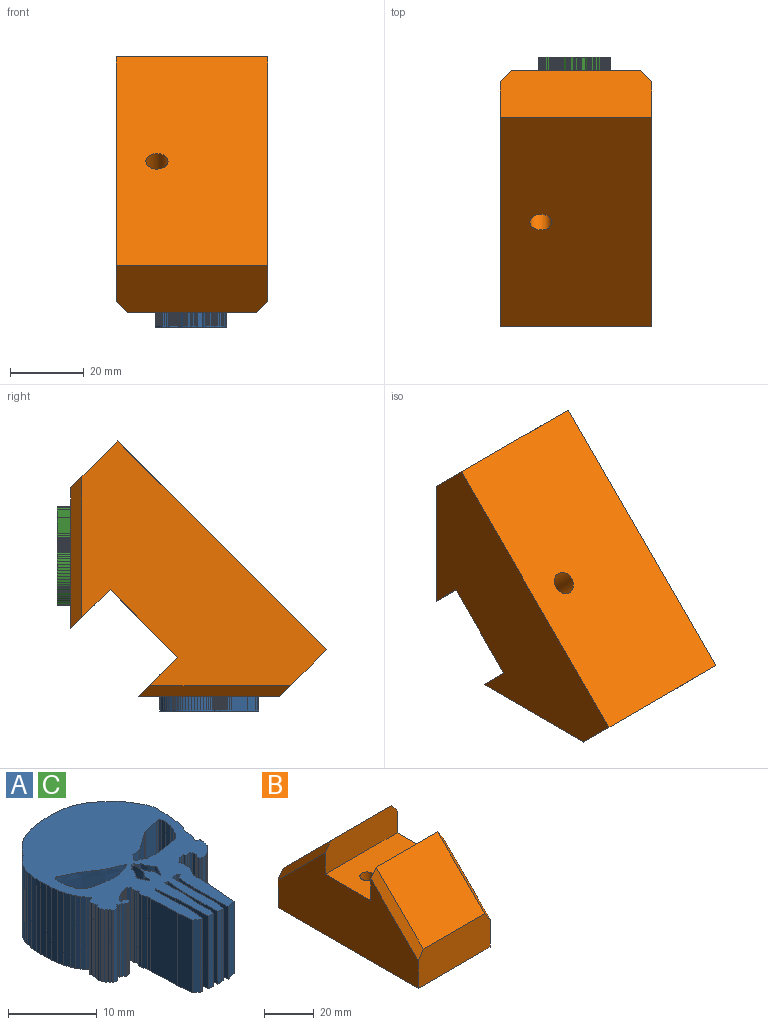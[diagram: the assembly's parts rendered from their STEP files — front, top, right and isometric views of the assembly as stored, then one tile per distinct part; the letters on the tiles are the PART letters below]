
ASSEMBLY  parts=3 mates=2
PART A: 224 faces, bbox 19.4x26.7x10 mm
  f0: plane 10x0.29mm, normal (0.2,0.98,0), area 3mm2, adj f1,f221,f222,f223
  f1: plane 10x0.83mm, normal (0.02,1,0), area 8.3mm2, adj f0,f2,f222,f223
  f2: plane 10x0.89mm, normal (0.48,0.88,0), area 10.2mm2, adj f1,f3,f222,f223
  f3: plane 10x0.29mm, normal (0.2,0.98,0), area 3mm2, adj f2,f4,f222,f223
  f4: plane 10x0.21mm, normal (0.5,0.87,0), area 2.4mm2, adj f3,f5,f222,f223
  f5: plane 10x0.29mm, normal (0.91,-0.42,0), area 3.2mm2, adj f4,f6,f222,f223
  f6: plane 10x0.67mm, normal (0.78,-0.63,0), area 8.6mm2, adj f5,f7,f222,f223
  f7: plane 10x1.25mm, normal (0.11,-0.99,0), area 12.6mm2, adj f6,f8,f222,f223
  f8: plane 10x2.46mm, normal (0.59,-0.81,0), area 30.5mm2, adj f7,f9,f222,f223
  f9: plane 10x0.51mm, normal (0.5,-0.87,0), area 5.9mm2, adj f8,f10,f222,f223
  f10: plane 10x2.19mm, normal (0.22,-0.98,0), area 22.4mm2, adj f9,f11,f222,f223
  f11: plane 10x0.54mm, normal (0.32,-0.95,0), area 5.7mm2, adj f10,f12,f222,f223
  f12: plane 10x0.41mm, normal (-0.94,-0.34,0), area 4.4mm2, adj f11,f13,f222,f223
  f13: plane 10x0.54mm, normal (-1,-0.08,0), area 5.4mm2, adj f12,f14,f222,f223
  f14: plane 10x0.97mm, normal (-0.99,0.12,0), area 9.7mm2, adj f13,f15,f222,f223
  f15: plane 10x0.7mm, normal (-0.92,0.38,0), area 7.6mm2, adj f14,f16,f222,f223
  f16: plane 10x0.26mm, normal (-0.79,0.61,0), area 3.3mm2, adj f15,f17,f222,f223
  f17: plane 10x0.69mm, normal (-0.88,0.47,0), area 7.8mm2, adj f16,f18,f222,f223
  f18: plane 10x0.56mm, normal (-0.67,0.75,0), area 7.4mm2, adj f17,f19,f222,f223
  f19: plane 10x0.72mm, normal (-0.22,0.98,0), area 7.3mm2, adj f18,f20,f222,f223
  f20: plane 10x0.7mm, normal (-0.12,0.99,0), area 7.1mm2, adj f19,f21,f222,f223
  f21: plane 10x1.19mm, normal (-0.18,0.98,0), area 12.1mm2, adj f20,f22,f222,f223
  f22: plane 10x0.7mm, normal (-0.12,0.99,0), area 7.1mm2, adj f21,f221,f222,f223
  f23: plane 10x0.35mm, normal (-0.2,-0.98,0), area 3.6mm2, adj f24,f217,f222,f223
  f24: plane 10x0.24mm, normal (-0.61,-0.79,0), area 3mm2, adj f23,f25,f222,f223
  f25: plane 10x0.19mm, normal (-0.67,-0.74,0), area 2.6mm2, adj f24,f26,f222,f223
  f26: plane 10x0.17mm, normal (-0.2,-0.98,0), area 1.8mm2, adj f25,f27,f222,f223
  f27: plane 10x0.2mm, normal (0.43,-0.9,0), area 2.2mm2, adj f26,f28,f222,f223
  f28: plane 10x0.15mm, normal (0.38,-0.93,0), area 1.6mm2, adj f27,f29,f222,f223
  f29: plane 10x0.16mm, normal (0.75,-0.66,0), area 2.1mm2, adj f28,f30,f222,f223
  f30: plane 10x0.29mm, normal (0.95,0.32,0), area 3mm2, adj f29,f31,f222,f223
  f31: plane 10x0.13mm, normal (0.86,0.51,0), area 1.5mm2, adj f30,f32,f222,f223
  f32: plane 10x0.53mm, normal (0.08,1,0), area 5.3mm2, adj f31,f33,f222,f223
  f33: plane 10x0.21mm, normal (0.83,0.56,0), area 2.5mm2, adj f32,f34,f222,f223
  f34: plane 10x0.34mm, normal (0.71,-0.71,0), area 4.8mm2, adj f33,f35,f222,f223
  f35: plane 10x0.17mm, normal (0.67,-0.75,0), area 2.2mm2, adj f34,f36,f222,f223
  f36: plane 10x0.11mm, normal (0.71,-0.71,0), area 1.6mm2, adj f35,f37,f222,f223
  f37: plane 10x0.41mm, normal (0.5,-0.87,0), area 4.7mm2, adj f36,f38,f222,f223
  f38: plane 10x0.21mm, normal (0.55,-0.83,0), area 2.5mm2, adj f37,f39,f222,f223
  f39: plane 10x0.25mm, normal (0.46,-0.89,0), area 2.8mm2, adj f38,f40,f222,f223
  f40: plane 10x0.24mm, normal (0.33,-0.94,0), area 2.6mm2, adj f39,f41,f222,f223
  f41: plane 10x0.28mm, normal (0.12,-0.99,0), area 2.8mm2, adj f40,f42,f222,f223
  f42: plane 10x0.2mm, normal (0.43,-0.9,0), area 2.2mm2, adj f41,f43,f222,f223
  f43: plane 10x0.22mm, normal (-0.2,-0.98,0), area 2.2mm2, adj f42,f44,f222,f223
  f44: plane 10x0.38mm, normal (-0.76,-0.65,0), area 5.1mm2, adj f43,f45,f222,f223
  f45: plane 10x0.11mm, normal (-0.71,0.71,0), area 1.6mm2, adj f44,f46,f222,f223
  f46: plane 10x0.22mm, normal (-0.98,0.19,0), area 2.2mm2, adj f45,f47,f222,f223
  f47: plane 10x0.14mm, normal (-0.99,-0.13,0), area 1.4mm2, adj f46,f48,f222,f223
  f48: plane 10x0.24mm, normal (-0.94,-0.34,0), area 2.6mm2, adj f47,f49,f222,f223
  f49: plane 10x0.16mm, normal (-0.83,-0.56,0), area 1.9mm2, adj f48,f50,f222,f223
  f50: plane 10x0.29mm, normal (-0.98,-0.18,0), area 2.9mm2, adj f49,f51,f222,f223
  f51: plane 10x0.28mm, normal (-0.51,0.86,0), area 3.2mm2, adj f50,f52,f222,f223
  f52: plane 10x0.54mm, normal (-1,0.03,0), area 5.4mm2, adj f51,f53,f222,f223
  f53: plane 10x0.67mm, normal (-0.96,-0.26,0), area 7mm2, adj f52,f54,f222,f223
  f54: plane 10x0.5mm, normal (-0.99,-0.13,0), area 5mm2, adj f53,f55,f222,f223
  f55: plane 10x4.16mm, normal (-1,-0.03,0), area 41.6mm2, adj f54,f56,f222,f223
  f56: plane 10x2.17mm, normal (-0.99,-0.11,0), area 21.8mm2, adj f55,f57,f222,f223
  f57: plane 10x0.67mm, normal (-0.63,-0.78,0), area 8.6mm2, adj f56,f58,f222,f223
  f58: plane 10x0.32mm, normal (-0.33,-0.94,0), area 3.4mm2, adj f57,f59,f222,f223
  f59: plane 10x0.34mm, normal (0.98,-0.22,0), area 3.5mm2, adj f58,f60,f222,f223
  f60: plane 10x2.27mm, normal (1,-0.08,0), area 22.8mm2, adj f59,f61,f222,f223
  f61: plane 10x5.04mm, normal (1,0.03,0), area 50.4mm2, adj f60,f62,f222,f223
  f62: plane 10x0.3mm, normal (0.78,-0.63,0), area 3.9mm2, adj f61,f63,f222,f223
  f63: plane 10x0.59mm, normal (-1,-0.03,0), area 5.9mm2, adj f62,f64,f222,f223
  f64: plane 10x2.29mm, normal (-0.99,-0.11,0), area 23mm2, adj f63,f65,f222,f223
  f65: plane 10x5.15mm, normal (-1,-0.03,0), area 51.6mm2, adj f64,f66,f222,f223
  f66: plane 10x0.81mm, normal (-0.08,-1,0), area 8.1mm2, adj f65,f67,f222,f223
  f67: plane 10x0.83mm, normal (0.96,-0.27,0), area 8.6mm2, adj f66,f68,f222,f223
  f68: plane 10x1.89mm, normal (1,0.03,0), area 18.9mm2, adj f67,f69,f222,f223
  f69: plane 10x2.5mm, normal (1,-0.08,0), area 25.1mm2, adj f68,f70,f222,f223
  f70: plane 10x2.95mm, normal (1,0.03,0), area 29.5mm2, adj f69,f71,f222,f223
  f71: plane 10x0.47mm, normal (0.01,-1,0), area 4.7mm2, adj f70,f72,f222,f223
  f72: plane 10x2.95mm, normal (-1,0.08,0), area 29.6mm2, adj f71,f73,f222,f223
  f73: plane 10x2.56mm, normal (-1,-0.03,0), area 25.6mm2, adj f72,f74,f222,f223
  f74: plane 10x2.68mm, normal (-1,0,0), area 26.8mm2, adj f73,f75,f222,f223
  f75: plane 10x0.61mm, normal (-0.08,-1,0), area 6.1mm2, adj f74,f76,f222,f223
  f76: plane 10x0.3mm, normal (0.09,-1,0), area 3mm2, adj f75,f77,f222,f223
  f77: plane 10x0.76mm, normal (0.98,-0.22,0), area 7.8mm2, adj f76,f78,f222,f223
  f78: plane 10x1.25mm, normal (1,-0.08,0), area 12.5mm2, adj f77,f79,f222,f223
  f79: plane 10x0.91mm, normal (0.99,0.11,0), area 9.1mm2, adj f78,f80,f222,f223
  f80: plane 10x5.38mm, normal (1,0,0), area 53.8mm2, adj f79,f81,f222,f223
  f81: plane 10x0.76mm, normal (0.24,-0.97,0), area 7.8mm2, adj f80,f82,f222,f223
  f82: plane 10x0.35mm, normal (-0.71,-0.7,0), area 4.9mm2, adj f81,f83,f222,f223
  f83: plane 10x0.6mm, normal (-0.45,0.9,0), area 6.7mm2, adj f82,f84,f222,f223
  f84: plane 10x2.57mm, normal (-1,0.08,0), area 25.8mm2, adj f83,f85,f222,f223
  f85: plane 10x5.39mm, normal (-1,-0.03,0), area 53.9mm2, adj f84,f86,f222,f223
  f86: plane 10x1.22mm, normal (0.22,-0.98,0), area 12.5mm2, adj f85,f87,f222,f223
  f87: plane 10x4.58mm, normal (1,-0.08,0), area 45.9mm2, adj f86,f88,f222,f223
  f88: plane 10x2.21mm, normal (1,0,0), area 22.1mm2, adj f87,f89,f222,f223
  f89: plane 10x0.72mm, normal (0.87,-0.5,0), area 8.3mm2, adj f88,f90,f222,f223
  f90: plane 10x0.34mm, normal (0.96,-0.29,0), area 3.5mm2, adj f89,f91,f222,f223
  f91: plane 10x0.33mm, normal (0.78,-0.63,0), area 4.3mm2, adj f90,f92,f222,f223
  f92: plane 10x0.65mm, normal (1,0,0), area 6.5mm2, adj f91,f93,f222,f223
  f93: plane 10x0.4mm, normal (1,0.09,0), area 4mm2, adj f92,f94,f222,f223
  f94: plane 10x0.55mm, normal (0.98,0.22,0), area 5.6mm2, adj f93,f95,f222,f223
  f95: plane 10x0.26mm, normal (0.55,-0.83,0), area 3.2mm2, adj f94,f96,f222,f223
  f96: plane 10x0.28mm, normal (0.67,-0.75,0), area 3.7mm2, adj f95,f97,f222,f223
  f97: plane 10x0.18mm, normal (0.55,-0.83,0), area 2.1mm2, adj f96,f98,f222,f223
  f98: plane 10x0.32mm, normal (0.26,-0.97,0), area 3.3mm2, adj f97,f99,f222,f223
  f99: plane 10x0.38mm, normal (0,-1,0), area 3.8mm2, adj f98,f100,f222,f223
  f100: plane 10x0.27mm, normal (-1,0.08,0), area 2.7mm2, adj f99,f101,f222,f223
  f101: plane 10x0.34mm, normal (-0.08,-1,0), area 3.4mm2, adj f100,f102,f222,f223
  f102: plane 10x0.42mm, normal (0.22,-0.98,0), area 4.2mm2, adj f101,f103,f222,f223
  f103: plane 10x0.23mm, normal (-0.63,-0.78,0), area 2.9mm2, adj f102,f104,f222,f223
  f104: plane 10x0.46mm, normal (-0.99,-0.11,0), area 4.6mm2, adj f103,f105,f222,f223
  f105: plane 10x0.18mm, normal (-1,-0.03,0), area 1.8mm2, adj f104,f106,f222,f223
  f106: plane 10x0.11mm, normal (-0.7,0.71,0), area 1.5mm2, adj f105,f107,f222,f223
  f107: plane 10x0.09mm, normal (-0.65,0.76,0), area 1.2mm2, adj f106,f108,f222,f223
  f108: plane 10x0.04mm, normal (-0.86,0.51,0), area 0.4mm2, adj f107,f109,f222,f223
  f109: plane 10x0.22mm, normal (-0.87,0.49,0), area 2.5mm2, adj f108,f110,f222,f223
  f110: plane 10x0.22mm, normal (-0.9,-0.45,0), area 2.4mm2, adj f109,f111,f222,f223
  f111: plane 10x0.02mm, normal (-0.84,-0.54,0), area 0.3mm2, adj f110,f112,f222,f223
  f112: plane 10x0.16mm, normal (-0.49,-0.87,0), area 1.8mm2, adj f111,f113,f222,f223
  f113: plane 10x0.07mm, normal (-0.71,-0.7,0), area 1mm2, adj f112,f114,f222,f223
  f114: plane 10x0.13mm, normal (-0.22,-0.98,0), area 1.3mm2, adj f113,f115,f222,f223
  f115: plane 10x0.34mm, normal (-0.08,-1,0), area 3.4mm2, adj f114,f116,f222,f223
  f116: plane 10x0.08mm, normal (0.59,-0.81,0), area 1mm2, adj f115,f117,f222,f223
  f117: plane 10x0.11mm, normal (-0.08,-1,0), area 1.1mm2, adj f116,f118,f222,f223
  f118: plane 10x0.11mm, normal (0.4,-0.92,0), area 1.2mm2, adj f117,f119,f222,f223
  f119: plane 10x0.34mm, normal (0.59,-0.81,0), area 4.2mm2, adj f118,f120,f222,f223
  f120: plane 10x0.22mm, normal (0.7,-0.71,0), area 3.2mm2, adj f119,f121,f222,f223
  f121: plane 10x0.39mm, normal (0.59,-0.81,0), area 4.8mm2, adj f120,f122,f222,f223
  f122: plane 10x0.28mm, normal (0.7,-0.71,0), area 4mm2, adj f121,f123,f222,f223
  f123: plane 10x0.15mm, normal (0.84,-0.54,0), area 1.7mm2, adj f122,f124,f222,f223
  f124: plane 10x0.16mm, normal (0.9,-0.43,0), area 1.7mm2, adj f123,f125,f222,f223
  f125: plane 10x0.35mm, normal (0.98,-0.22,0), area 3.5mm2, adj f124,f126,f222,f223
  f126: plane 10x0.32mm, normal (0.96,-0.27,0), area 3.4mm2, adj f125,f127,f222,f223
  f127: plane 10x0.39mm, normal (0.99,-0.12,0), area 4mm2, adj f126,f128,f222,f223
  f128: plane 10x0.03mm, normal (0.81,0.59,0), area 0.4mm2, adj f127,f129,f222,f223
  f129: plane 10x0.04mm, normal (0.94,-0.33,0), area 0.5mm2, adj f128,f130,f222,f223
  f130: plane 10x0.02mm, normal (0.84,0.54,0), area 0.3mm2, adj f129,f131,f222,f223
  f131: plane 10x0.09mm, normal (0.92,0.4,0), area 0.9mm2, adj f130,f132,f222,f223
  f132: plane 10x0.08mm, normal (0.73,0.68,0), area 1.2mm2, adj f131,f133,f222,f223
  f133: plane 10x0.2mm, normal (0.12,0.99,0), area 2mm2, adj f132,f134,f222,f223
  f134: plane 10x0.06mm, normal (0.22,0.98,0), area 0.6mm2, adj f133,f135,f222,f223
  f135: plane 10x0.05mm, normal (0.71,0.7,0), area 0.7mm2, adj f134,f136,f222,f223
  f136: plane 10x0.06mm, normal (0.92,0.4,0), area 0.7mm2, adj f135,f137,f222,f223
  f137: plane 10x0.07mm, normal (0.98,0.22,0), area 0.7mm2, adj f136,f138,f222,f223
  f138: plane 10x0.61mm, normal (0.93,-0.36,0), area 6.6mm2, adj f137,f139,f222,f223
  f139: plane 10x0.63mm, normal (0.98,-0.22,0), area 6.5mm2, adj f138,f140,f222,f223
  f140: plane 10x0.63mm, normal (1,-0.08,0), area 6.3mm2, adj f139,f141,f222,f223
  f141: plane 10x1.27mm, normal (0.94,-0.33,0), area 13.5mm2, adj f140,f142,f222,f223
  f142: plane 10x1.31mm, normal (0.98,-0.22,0), area 13.5mm2, adj f141,f143,f222,f223
  f143: plane 10x1.36mm, normal (1,-0.08,0), area 13.6mm2, adj f142,f144,f222,f223
  f144: plane 10x1.33mm, normal (1,0,0), area 13.3mm2, adj f143,f145,f222,f223
  f145: plane 10x0.29mm, normal (0.99,-0.12,0), area 2.9mm2, adj f144,f146,f222,f223
  f146: plane 10x0.58mm, normal (0.99,0.11,0), area 5.8mm2, adj f145,f147,f222,f223
  f147: plane 10x0.28mm, normal (0.98,0.22,0), area 2.8mm2, adj f146,f148,f222,f223
  f148: plane 10x0.52mm, normal (0.92,0.4,0), area 5.7mm2, adj f147,f149,f222,f223
  f149: plane 10x0.23mm, normal (0.81,0.59,0), area 2.9mm2, adj f148,f150,f222,f223
  f150: plane 10x0.89mm, normal (0.9,0.45,0), area 9.9mm2, adj f149,f151,f222,f223
  f151: plane 10x0.83mm, normal (0.84,0.54,0), area 9.9mm2, adj f150,f152,f222,f223
  f152: plane 10x0.79mm, normal (0.79,0.62,0), area 10mm2, adj f151,f153,f222,f223
  f153: plane 10x0.7mm, normal (0.71,0.7,0), area 9.8mm2, adj f152,f154,f222,f223
  f154: plane 10x0.75mm, normal (0.65,0.76,0), area 9.9mm2, adj f153,f155,f222,f223
  f155: plane 10x0.64mm, normal (0.64,0.76,0), area 8.3mm2, adj f154,f156,f222,f223
  f156: plane 10x0.68mm, normal (0.56,0.83,0), area 8.2mm2, adj f155,f157,f222,f223
  f157: plane 10x0.74mm, normal (0.46,0.89,0), area 8.4mm2, adj f156,f158,f222,f223
  f158: plane 10x0.76mm, normal (0.37,0.93,0), area 8.1mm2, adj f157,f159,f222,f223
  f159: plane 10x0.81mm, normal (0.25,0.97,0), area 8.4mm2, adj f158,f160,f222,f223
  f160: plane 10x1.3mm, normal (0.15,0.99,0), area 13.1mm2, adj f159,f161,f222,f223
  f161: plane 10x1.3mm, normal (0.03,1,0), area 13mm2, adj f160,f162,f222,f223
  f162: plane 10x1.31mm, normal (-0.08,1,0), area 13.2mm2, adj f161,f163,f222,f223
  f163: plane 10x0.89mm, normal (-0.08,1,0), area 8.9mm2, adj f162,f164,f222,f223
  f164: plane 10x0.87mm, normal (-0.19,0.98,0), area 8.8mm2, adj f163,f165,f222,f223
  f165: plane 10x0.86mm, normal (-0.29,0.96,0), area 9mm2, adj f164,f166,f222,f223
  f166: plane 10x0.82mm, normal (-0.4,0.92,0), area 9mm2, adj f165,f167,f222,f223
  f167: plane 10x0.77mm, normal (-0.55,0.83,0), area 9.2mm2, adj f166,f168,f222,f223
  f168: plane 10x0.69mm, normal (-0.64,0.77,0), area 9mm2, adj f167,f169,f222,f223
  f169: plane 10x0.66mm, normal (-0.72,0.69,0), area 9.2mm2, adj f168,f170,f222,f223
  f170: plane 10x0.72mm, normal (-0.79,0.62,0), area 9.2mm2, adj f169,f171,f222,f223
  f171: plane 10x0.4mm, normal (-0.55,0.83,0), area 4.8mm2, adj f170,f172,f222,f223
  f172: plane 10x0.36mm, normal (-0.65,0.76,0), area 4.8mm2, adj f171,f173,f222,f223
  f173: plane 10x0.35mm, normal (-0.74,0.67,0), area 4.8mm2, adj f172,f174,f222,f223
  f174: plane 10x0.38mm, normal (-0.83,0.56,0), area 4.7mm2, adj f173,f175,f222,f223
  f175: plane 10x0.41mm, normal (-0.87,0.49,0), area 4.8mm2, adj f174,f176,f222,f223
  f176: plane 10x0.45mm, normal (-0.93,0.36,0), area 4.8mm2, adj f175,f177,f222,f223
  f177: plane 10x0.45mm, normal (-0.97,0.25,0), area 4.7mm2, adj f176,f178,f222,f223
  f178: plane 10x0.79mm, normal (-0.97,0.23,0), area 8.1mm2, adj f177,f179,f222,f223
  f179: plane 10x0.8mm, normal (-0.99,0.13,0), area 8mm2, adj f178,f180,f222,f223
  f180: plane 10x0.81mm, normal (-1,0.03,0), area 8.1mm2, adj f179,f181,f222,f223
  f181: plane 10x0.8mm, normal (-1,-0.06,0), area 8mm2, adj f180,f182,f222,f223
  f182: plane 10x0.84mm, normal (-1,-0.03,0), area 8.4mm2, adj f181,f183,f222,f223
  f183: plane 10x0.83mm, normal (-0.99,-0.11,0), area 8.3mm2, adj f182,f184,f222,f223
  f184: plane 10x0.81mm, normal (-0.98,-0.22,0), area 8.3mm2, adj f183,f185,f222,f223
  f185: plane 10x0.8mm, normal (-0.96,-0.29,0), area 8.3mm2, adj f184,f186,f222,f223
  f186: plane 10x0.58mm, normal (-0.92,-0.4,0), area 6.4mm2, adj f185,f187,f222,f223
  f187: plane 10x0.55mm, normal (-0.86,-0.5,0), area 6.4mm2, adj f186,f188,f222,f223
  f188: plane 10x0.5mm, normal (-0.81,-0.59,0), area 6.2mm2, adj f187,f189,f222,f223
  f189: plane 10x0.46mm, normal (-0.73,-0.68,0), area 6.3mm2, adj f188,f190,f222,f223
  f190: plane 10x0.25mm, normal (-0.45,0.9,0), area 2.8mm2, adj f189,f191,f222,f223
  f191: plane 10x0.26mm, normal (-0.4,0.92,0), area 2.8mm2, adj f190,f192,f222,f223
  f192: plane 10x0.24mm, normal (-0.35,0.94,0), area 2.6mm2, adj f191,f193,f222,f223
  f193: plane 10x0.15mm, normal (-0.96,0.29,0), area 1.5mm2, adj f192,f194,f222,f223
  f194: plane 10x0.15mm, normal (-0.98,0.22,0), area 1.5mm2, adj f193,f195,f222,f223
  f195: plane 10x0.28mm, normal (-1,0,0), area 2.8mm2, adj f194,f196,f222,f223
  f196: plane 10x0.15mm, normal (-0.98,-0.22,0), area 1.5mm2, adj f195,f197,f222,f223
  f197: plane 10x0.13mm, normal (-0.99,-0.16,0), area 1.3mm2, adj f196,f198,f222,f223
  f198: plane 10x0.27mm, normal (-0.9,-0.45,0), area 3mm2, adj f197,f199,f222,f223
  f199: plane 10x0.15mm, normal (-0.83,0.56,0), area 1.8mm2, adj f198,f200,f222,f223
  f200: plane 10x0.14mm, normal (-0.45,0.9,0), area 1.6mm2, adj f199,f201,f222,f223
  f201: plane 10x0.13mm, normal (-0.96,0.29,0), area 1.3mm2, adj f200,f202,f222,f223
  f202: plane 10x0.38mm, normal (-1,0,0), area 3.8mm2, adj f201,f203,f222,f223
  f203: plane 10x0.13mm, normal (-0.9,-0.45,0), area 1.5mm2, adj f202,f204,f222,f223
  f204: plane 10x0.11mm, normal (-1,0,0), area 1.1mm2, adj f203,f205,f222,f223
  f205: plane 10x0.12mm, normal (-0.89,-0.45,0), area 1.3mm2, adj f204,f206,f222,f223
  f206: plane 10x0.11mm, normal (-0.87,-0.49,0), area 1.2mm2, adj f205,f207,f222,f223
  f207: plane 10x0.1mm, normal (-0.75,-0.66,0), area 1.3mm2, adj f206,f208,f222,f223
  f208: plane 10x0.1mm, normal (-0.71,-0.71,0), area 1.4mm2, adj f207,f209,f222,f223
  f209: plane 10x0.12mm, normal (-0.51,-0.86,0), area 1.4mm2, adj f208,f210,f222,f223
  f210: plane 10x0.18mm, normal (-0.95,-0.32,0), area 1.9mm2, adj f209,f211,f222,f223
  f211: plane 10x0.15mm, normal (-0.77,-0.64,0), area 1.9mm2, adj f210,f212,f222,f223
  f212: plane 10x0.15mm, normal (-0.86,-0.5,0), area 1.7mm2, adj f211,f213,f222,f223
  f213: plane 10x0.15mm, normal (-0.71,-0.71,0), area 2mm2, adj f212,f214,f222,f223
  f214: plane 10x0.51mm, normal (0,-1,0), area 5.1mm2, adj f213,f215,f222,f223
  f215: plane 10x0.49mm, normal (0.76,-0.66,0), area 6.4mm2, adj f214,f217,f222,f223
  f216: extruded ~10x3.69mm, area 66.7mm2, adj f220,f222,f223
  f217: plane 10x0.19mm, normal (-0.67,-0.74,0), area 2.6mm2, adj f23,f215,f222,f223
  f218: extruded ~10x7.59mm, area 203.8mm2, adj f222,f223
  f219: extruded ~10x3.54mm, area 83.4mm2, adj f222,f223
  f220: extruded ~10x1.92mm, area 19.4mm2, adj f216,f222,f223
  f221: plane 10x0.45mm, normal (0.04,1,0), area 4.5mm2, adj f0,f22,f222,f223
  f222: plane 26.75x19.35mm, normal (0,0,1), area 292.7mm2, adj f0,f1,f2,f3,f4,f5,f6,f7
  f223: plane 26.75x19.35mm, normal (0,0,-1), area 292.7mm2, adj f0,f1,f2,f3,f4,f5,f6,f7
PART B: 15 faces, bbox 41x80x45 mm
  f0: plane 80x40.76mm, normal (-1,0,0), area 2251.9mm2, adj f3,f4,f5,f6,f8,f9,f12,f14
  f1: plane 80x40.76mm, normal (1,0,0), area 2251.9mm2, adj f3,f4,f5,f6,f8,f9,f11,f13
  f2: cylinder r=3mm len=30mm, axis (0,0,-1), area 565.5mm2, adj f3,f4
  f3: plane 41x26mm, normal (0,0,1), area 1037.7mm2, adj f0,f1,f2,f5,f8
  f4: plane 80x41mm, normal (0,0,-1), area 3251.7mm2, adj f0,f1,f2,f6,f9
  f5: plane 41x15mm, normal (0,-1,0), area 602.3mm2, adj f0,f1,f3,f7,f11,f12
  f6: plane 41x18mm, normal (0,1,0), area 725.3mm2, adj f0,f1,f4,f7,f11,f12
  f7: plane 35x27mm, normal (0,0.71,0.71), area 1336.4mm2, adj f5,f6,f11,f12
  f8: plane 41x15mm, normal (0,1,0), area 602.3mm2, adj f0,f1,f3,f10,f13,f14
  f9: plane 41x18mm, normal (0,-1,0), area 725.3mm2, adj f0,f1,f4,f10,f13,f14
  f10: plane 35x27mm, normal (0,-0.71,0.71), area 1336.4mm2, adj f8,f9,f13,f14
  f11: plane 31.24x27mm, normal (0.71,0.5,0.5), area 162mm2, adj f1,f5,f6,f7
  f12: plane 31.24x27mm, normal (-0.71,0.5,0.5), area 162mm2, adj f0,f5,f6,f7
  f13: plane 31.24x27mm, normal (0.71,-0.5,0.5), area 162mm2, adj f1,f8,f9,f10
  f14: plane 31.24x27mm, normal (-0.71,-0.5,0.5), area 162mm2, adj f0,f8,f9,f10
PART C: same geometry as A
PLACE A t=(-157.15,25.79,-24.22)mm
PLACE B rot(axis=(-1,0,0),135deg) t=(-72.04,44.1,20.69)mm
PLACE C rot(axis=(-1,0,0),90deg) t=(-157.34,78.76,39.71)mm
MATE parallel B.f7 <-> A.f222  axis (0,0,-1) through (-62.54,47.64,-20.32)mm
MATE parallel B.f10 <-> C.f222  axis (0,1,0) through (-62.54,85.12,17.16)mm
